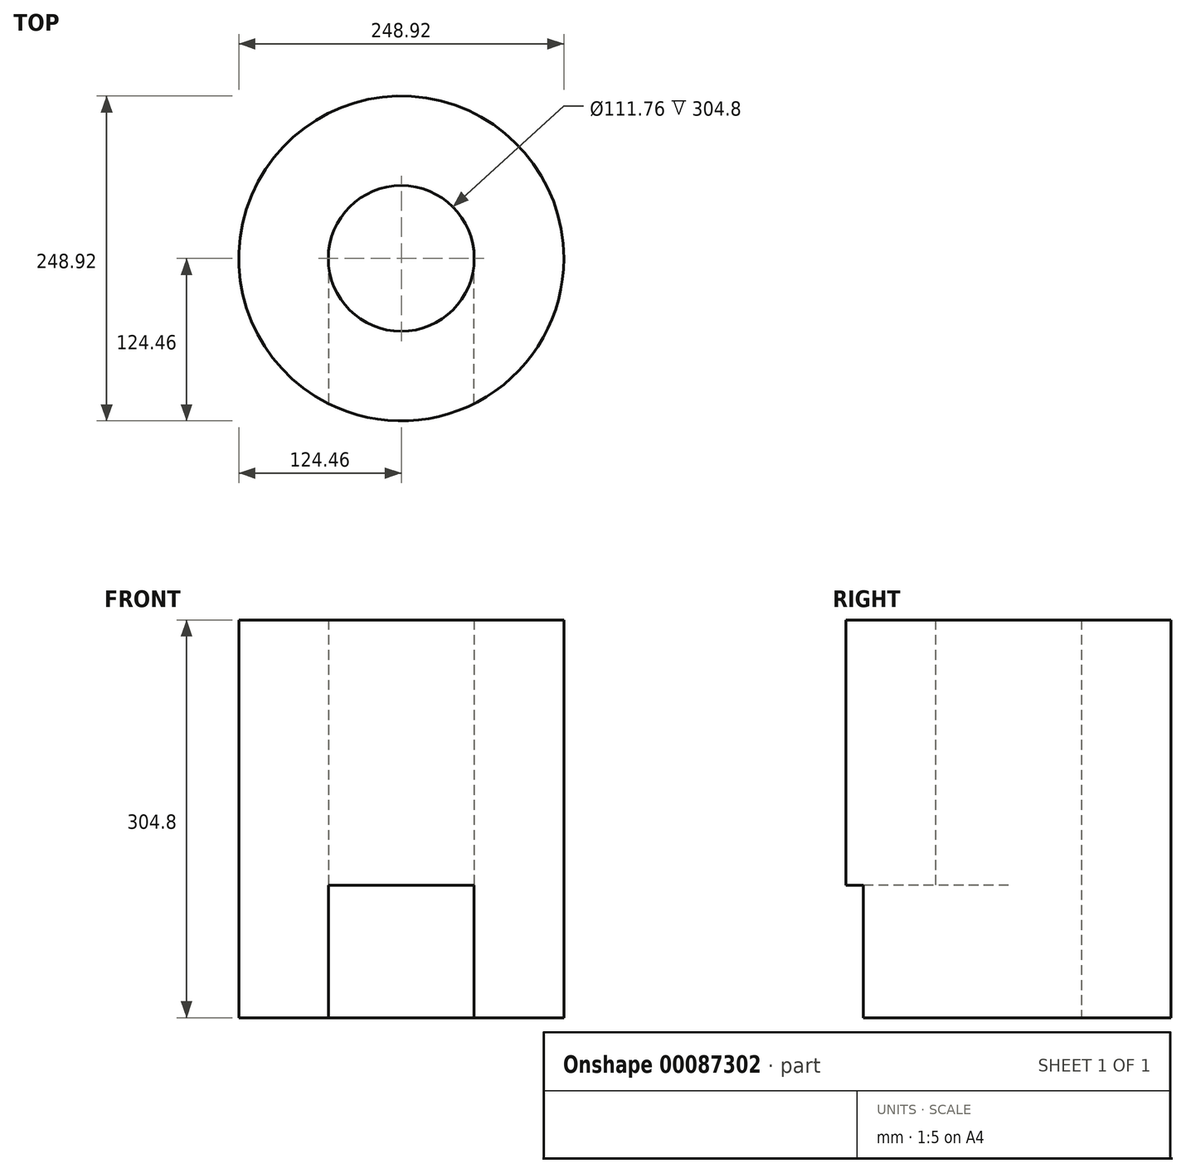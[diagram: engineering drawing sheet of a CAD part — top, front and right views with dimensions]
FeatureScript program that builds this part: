
annotation { "Feature Type Name" : "Feature", "Feature Type Description" : "" }
export const myFeature = defineFeature(function(context is Context, id is Id, definition is map)
    precondition{}
    {
        {
            var Q0;
            Q0=qCreatedBy(makeId("Top.planeOp"),FACE);
            var sketch = newSketch(context, id + "F0", { "sketchPlane" : qUnion([Q0])});
            skCircle(sketch, "E0", {"center": v(0, 0) * mm, "radius": 124.46 * mm});
            skCircle(sketch, "E1", {"center": v(0, 0) * mm, "radius": 55.88 * mm});
            skLineSegment(sketch, "E2", {"start": v(-55.88, 0) * mm, "end": v(-55.88, -111.21) * mm});
            skLineSegment(sketch, "E3", {"start": v(55.88, -111.21) * mm, "end": v(55.88, 0) * mm});
            skSolve(sketch);
        }
        {
            var Q0;
            Q0 = qSketchRegion(id + "F0", true);
            extrude(context, id + "F1", {"entities" : qUnion([Q0]), "depth" : 304.8 * mm});
        }
        {
            var Q0;
            {var subQ0=sQuery(id+"F0.wireOp",EDGE,"E2");Q0=makeQuery(id+"F0.imprint","IMPRINT",FACE,{"disambiguationData":[TD([[makeQuery(id+"F0.imprint","IMPRINT",EDGE,{"derivedFrom":subQ0}),1.0]])]});}
            extrude(context, id + "F2", {"entities" : qUnion([Q0]), "operationType" : NewBodyOperationType.REMOVE, "depth" : 101.6 * mm});
        }
    });
